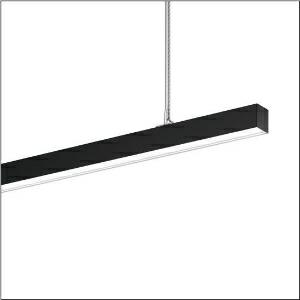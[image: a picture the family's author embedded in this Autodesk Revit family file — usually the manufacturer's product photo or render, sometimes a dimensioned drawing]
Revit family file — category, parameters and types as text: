
# Revit family: silica_r__21_51mx30da44bb_2b52
name_source: partatom
category: Lighting Fixtures
units: mm (PartAtom-declared; Revit-internal decimal feet)

## family parameters
Cut with Voids When Loaded = No
Host = Face
Light Source = No
Part Type = Normal
Room Calculation Point = No
Round Connector Dimension = Use Diameter
Shared = No

## types (1)
- --- (1 x LED, 4210 lm, 26 W, 4000K)
    Apparent Load = 26 VA
    CIE Flux Codes = 47 79 96 57 100
    Color Rendering = 80
    Color Temperature = 4000K
    Default Elevation = 1800 mm
    Description = Silica® 21, office luminaire, primary optical cover: cover, of PMMA, opal, light emission: direct/indirect distribution, primary light characteristic: symmetric, installation type: suspended mounting, LED, rated luminous flux: 4.210lm, luminous efficacy: 162lm/W, light colour: 840, colour temperature: 4000K, with terminal, 3+2-pole, max. 2.5mm², mains connection: 220..240V, AC, 50/60Hz, rated input power: 26W, luminaire housing, of aluminium, jet black (RAL 9005), length: 1.204mm, width: 53mm, height: 53mm, protection rating (complete): IP20, insulation class (complete): insulation class I (protective earthing), certification: CE, permissible operating ambient temperature: 0..+35°C, standard: EN 50419, packaging unit: 1 piece
    Height = 53 mm
    Lamp = 1 x LED
    Lamp Light Flux = 4210 lm
    Lamp Power = 26 W
    Lamp count = 1
    Length = 1204 mm
    Luminous efficacy = 162 lm/W
    Manufacturer = Siteco
    ModVariant = No
    Model = 51MX30DA44BB
    Mounting Place = Ceiling
    Mounting Type = Pendant
    Number of Poles = 1
    OnlyDefault = Yes
    Power Factor = 1
    Product Name = Silica® 21
    Product group = office luminaire | ceiling pendant
    ProductGroupID = 905
    Protection Class = Protection class I
    Protection Degree = IP 20
    RLX_Detail_Level = 1
    RlxData = <blob elided: 25765 chars, md5=2e6e4670>
    Socket = socket
    Standby Power = 0 W
    System Light Flux = 4210 lm
    System Power = 26 W
    Type Comments = factory setting: luminous flux: 100 % | dim-lin: 254 | 218 mA
    Type Image = l_1251735.jpg
    URL = http://relux.com
    VarID = @adj_025753
    Voltage = 0 V
    Weight = 0.00 kg
    Width = 53 mm

## geometry (parser evidence)
native form markers: Blend x4, Sweep x15
no freeform markers — native parametric forms only
